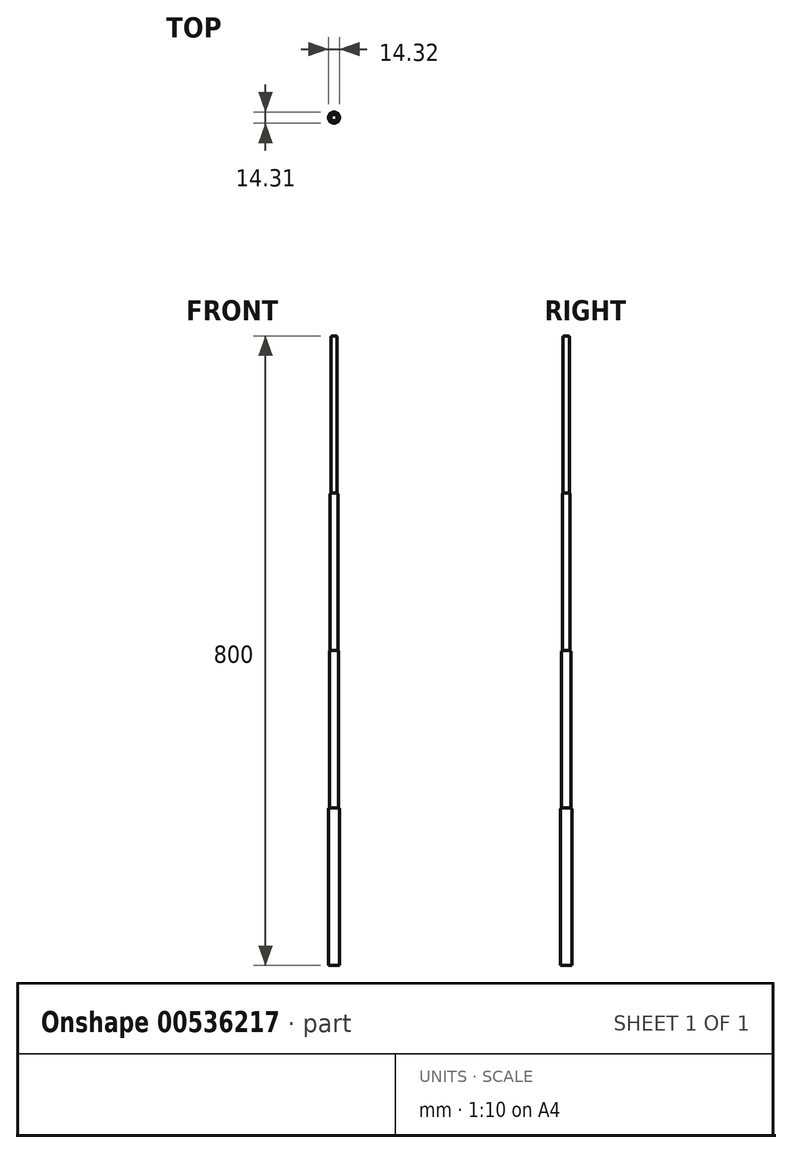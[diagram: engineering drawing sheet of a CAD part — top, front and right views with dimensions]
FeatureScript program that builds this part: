
annotation { "Feature Type Name" : "Feature", "Feature Type Description" : "" }
export const myFeature = defineFeature(function(context is Context, id is Id, definition is map)
    precondition{}
    {
        {
            var Q0;
            Q0=qCreatedBy(makeId("Top.planeOp"),FACE);
            var sketch = newSketch(context, id + "F0", { "sketchPlane" : qUnion([Q0])});
            skCircle(sketch, "E0", {"center": v(231.38, 15.82) * mm, "radius": 7.16 * mm});
            skCircle(sketch, "E1", {"center": v(231.38, 15.82) * mm, "radius": 6 * mm});
            skCircle(sketch, "E2", {"center": v(231.38, 15.82) * mm, "radius": 5 * mm});
            skCircle(sketch, "E3", {"center": v(231.38, 15.82) * mm, "radius": 4 * mm});
            skSolve(sketch);
        }
        {
            var Q0;
            Q0 = qSketchRegion(id + "F0", true);
            var Q1;
            Q1=makeQuery(id+"F0.imprint","IMPRINT",FACE,{"disambiguationData":[TD([[makeQuery(id+"F0.imprint","IMPRINT",EDGE,{"derivedFrom":sQuery(id+"F0.wireOp",EDGE,"E1")}),1.0]])]});
            var Q2;
            Q2=makeQuery(id+"F0.imprint","IMPRINT",FACE,{"disambiguationData":[TD([[makeQuery(id+"F0.imprint","IMPRINT",EDGE,{"derivedFrom":sQuery(id+"F0.wireOp",EDGE,"E2")}),1.0]])]});
            var Q3;
            Q3=makeQuery(id+"F0.imprint","IMPRINT",FACE,{"disambiguationData":[TD([[makeQuery(id+"F0.imprint","IMPRINT",EDGE,{"derivedFrom":sQuery(id+"F0.wireOp",EDGE,"E3")}),1.0]])]});
            extrude(context, id + "F1", {"entities" : qUnion([Q0, Q1, Q2, Q3]), "depth" : 200 * mm, "offsetDistance" : 25 * mm});
        }
        {
            var Q0;
            Q0=makeQuery(id+"F0.imprint","IMPRINT",FACE,{"disambiguationData":[TD([[makeQuery(id+"F0.imprint","IMPRINT",EDGE,{"derivedFrom":sQuery(id+"F0.wireOp",EDGE,"E1")}),1.0]])]});
            var Q1;
            Q1=makeQuery(id+"F0.imprint","IMPRINT",FACE,{"disambiguationData":[TD([[makeQuery(id+"F0.imprint","IMPRINT",EDGE,{"derivedFrom":sQuery(id+"F0.wireOp",EDGE,"E2")}),1.0]])]});
            var Q2;
            Q2=makeQuery(id+"F0.imprint","IMPRINT",FACE,{"disambiguationData":[TD([[makeQuery(id+"F0.imprint","IMPRINT",EDGE,{"derivedFrom":sQuery(id+"F0.wireOp",EDGE,"E3")}),1.0]])]});
            extrude(context, id + "F2", {"entities" : qUnion([Q0, Q1, Q2]), "operationType" : NewBodyOperationType.ADD, "depth" : 400 * mm, "offsetDistance" : 25 * mm});
        }
        {
            var Q0;
            Q0=makeQuery(id+"F0.imprint","IMPRINT",FACE,{"disambiguationData":[TD([[makeQuery(id+"F0.imprint","IMPRINT",EDGE,{"derivedFrom":sQuery(id+"F0.wireOp",EDGE,"E2")}),1.0]])]});
            var Q1;
            Q1=makeQuery(id+"F0.imprint","IMPRINT",FACE,{"disambiguationData":[TD([[makeQuery(id+"F0.imprint","IMPRINT",EDGE,{"derivedFrom":sQuery(id+"F0.wireOp",EDGE,"E3")}),1.0]])]});
            extrude(context, id + "F3", {"entities" : qUnion([Q0, Q1]), "operationType" : NewBodyOperationType.ADD, "depth" : 600 * mm, "offsetDistance" : 25 * mm});
        }
        {
            var Q0;
            Q0=makeQuery(id+"F0.imprint","IMPRINT",FACE,{"disambiguationData":[TD([[makeQuery(id+"F0.imprint","IMPRINT",EDGE,{"derivedFrom":sQuery(id+"F0.wireOp",EDGE,"E3")}),1.0]])]});
            extrude(context, id + "F4", {"entities" : qUnion([Q0]), "operationType" : NewBodyOperationType.ADD, "depth" : 800 * mm, "offsetDistance" : 25 * mm});
        }
        {
            var Q0;
            Q0=makeQuery(id+"F1.opExtrude","CAP_EDGE",EDGE,{"disambiguationData":[OSD([sQuery(id+"F0.wireOp",EDGE,"E0")])],"isStart":false});
            var Q1;
            Q1=makeQuery(id+"F2.opExtrude","CAP_EDGE",EDGE,{"disambiguationData":[OSD([sQuery(id+"F0.wireOp",EDGE,"E1")])],"isStart":false});
            var Q2;
            Q2=makeQuery(id+"F3.opExtrude","CAP_EDGE",EDGE,{"disambiguationData":[OSD([sQuery(id+"F0.wireOp",EDGE,"E2")])],"isStart":false});
            var Q3;
            Q3=makeQuery(id+"F4.opExtrude","CAP_EDGE",EDGE,{"disambiguationData":[OSD([sQuery(id+"F0.wireOp",EDGE,"E3")])],"isStart":false});
            fillet(context, id + "F5", {"entities" : qUnion([Q0, Q1, Q2, Q3]), "radius" : 2 * mm, "tangentPropagation" : true, "allowEdgeOverflow" : false});
        }
    });
